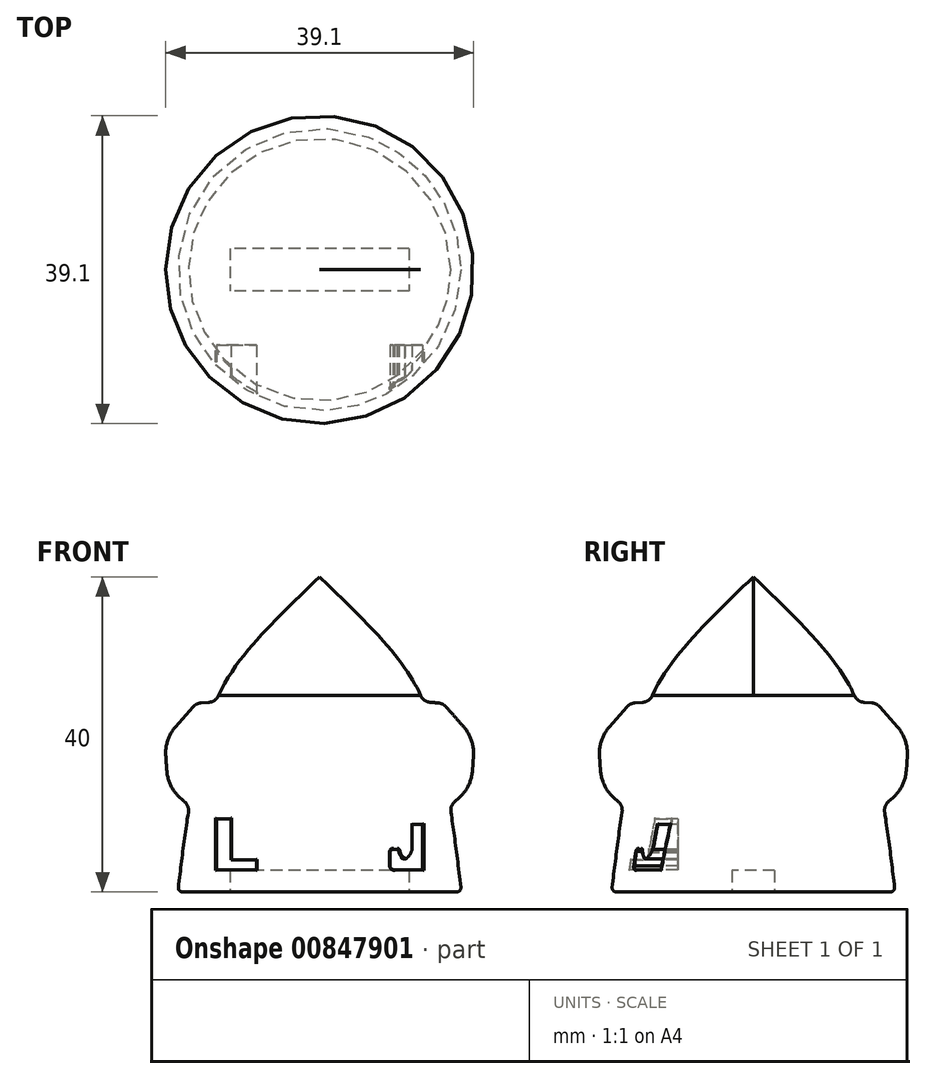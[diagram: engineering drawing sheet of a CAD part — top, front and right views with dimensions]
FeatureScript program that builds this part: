
annotation { "Feature Type Name" : "Feature", "Feature Type Description" : "" }
export const myFeature = defineFeature(function(context is Context, id is Id, definition is map)
    precondition{}
    {
        {
            var Q0;
            Q0=qCreatedBy(makeId("Front.planeOp"),FACE);
            var sketch = newSketch(context, id + "F0", { "sketchPlane" : qUnion([Q0])});
            skLineSegment(sketch, "E0", {"start": v(18, 0) * mm, "end": v(0, 0) * mm});
            skLineSegment(sketch, "E1", {"start": v(0, 40) * mm, "end": v(0, 0) * mm});
            skFitSpline(sketch, "E2", {"points": [v(18, 0) * mm, v(13.4, 23.62) * mm, v(0, 40) * mm], "startDerivative": vector(-8.21, 72.25) * mm, "endDerivative": vector(-57.18, 54.27) * mm});
            skPoint(sketch, "E3.center.orphan", {"position": v(0, 43.03) * mm});
            skFitSpline(sketch, "E4.trimOffspring", {"points": [v(18, 0) * mm, v(13.4, 23.62) * mm, v(0, 40) * mm], "startDerivative": vector(-8.21, 72.25) * mm, "endDerivative": vector(-57.18, 54.27) * mm});
            skArc(sketch, "E5.cCircle", {"start": v(16.55, 10.95) * mm, "mid": v(19.26, 18.64) * mm, "end": v(13.2, 24.1) * mm, "construction": true});
            skLineSegment(sketch, "E5.0", {"start": v(15.66, 23.96) * mm, "end": v(19.67, 19.38) * mm});
            skLineSegment(sketch, "E5.1", {"start": v(19.67, 19.38) * mm, "end": v(19.27, 13.3) * mm});
            skLineSegment(sketch, "E5.2", {"start": v(19.27, 13.3) * mm, "end": v(16.55, 10.93) * mm});
            skLineSegment(sketch, "E5.7", {"start": v(13.2, 24.13) * mm, "end": v(15.66, 23.96) * mm});
            skPoint(sketch, "E5.0.midPoint", {"position": v(17.67, 21.67) * mm});
            skPoint(sketch, "E6.orphan", {"position": v(9.6, 24.36) * mm});
            skSolve(sketch);
        }
        {
            var Q0;
            Q0 = qSketchRegion(id + "F0", true);
            var Q1;
            Q1=sQuery(id+"F0.wireOp",EDGE,"E1");
            revolve(context, id + "F1", {"surfaceOperationType" : NewSurfaceOperationType.NEW, "entities" : qUnion([Q0]), "axis" : qUnion([Q1]), "revolveType" : RevolveType.FULL});
        }
        {
            var Q0;
            Q0=qCreatedBy(makeId("Front.planeOp"),FACE);
            cPlane(context, id + "F2", {"entities" : qUnion([Q0]), "cplaneType" : CPlaneType.OFFSET, "offset" : 25 * mm, "width" : 150 * mm, "height" : 150 * mm});
        }
        {
            var Q0;
            Q0=makeQuery(id+"F1.opRevolve","SWEPT_EDGE",EDGE,{"disambiguationData":[OSD([sQuery(id+"F0.wireOp",EDGE,"E4.trimOffspring"),sQuery(id+"F0.wireOp",EDGE,"E5.7")])]});
            var Q1;
            Q1=makeQuery(id+"F1.opRevolve","SWEPT_EDGE",EDGE,{"disambiguationData":[OSD([sQuery(id+"F0.wireOp",EDGE,"E5.0"),sQuery(id+"F0.wireOp",EDGE,"E5.7")])]});
            var Q2;
            Q2=makeQuery(id+"F1.opRevolve","SWEPT_EDGE",EDGE,{"disambiguationData":[OSD([sQuery(id+"F0.wireOp",EDGE,"E2"),sQuery(id+"F0.wireOp",EDGE,"E5.2")])]});
            fillet(context, id + "F3", {"entities" : qUnion([Q0, Q1, Q2]), "radius" : 1.5 * mm, "tangentPropagation" : true, "allowEdgeOverflow" : false});
        }
        {
            var Q0;
            Q0=makeQuery(id+"F1.opRevolve","SWEPT_EDGE",EDGE,{"disambiguationData":[OSD([sQuery(id+"F0.wireOp",EDGE,"E5.0"),sQuery(id+"F0.wireOp",EDGE,"E5.1")])]});
            var Q1;
            Q1=makeQuery(id+"F1.opRevolve","SWEPT_EDGE",EDGE,{"disambiguationData":[OSD([sQuery(id+"F0.wireOp",EDGE,"E5.1"),sQuery(id+"F0.wireOp",EDGE,"E5.2")])]});
            fillet(context, id + "F4", {"entities" : qUnion([Q0, Q1]), "radius" : 5 * mm, "tangentPropagation" : true, "allowEdgeOverflow" : false});
        }
        {
            var Q0;
            Q0=qCreatedBy(makeId("Top.planeOp"),FACE);
            var sketch = newSketch(context, id + "F5", { "sketchPlane" : qUnion([Q0])});
            skLineSegment(sketch, "E7.bottom", {"start": v(11.37, 2.7) * mm, "end": v(-11.37, 2.7) * mm});
            skLineSegment(sketch, "E7.top", {"start": v(11.37, -2.7) * mm, "end": v(-11.37, -2.7) * mm});
            skLineSegment(sketch, "E7.left", {"start": v(11.37, 2.7) * mm, "end": v(11.37, -2.7) * mm});
            skLineSegment(sketch, "E7.right", {"start": v(-11.37, 2.7) * mm, "end": v(-11.37, -2.7) * mm});
            skPoint(sketch, "E7.middle", {"position": v(0, 0) * mm});
            skSolve(sketch);
        }
        {
            var Q0;
            Q0 = qSketchRegion(id + "F5", true);
            extrude(context, id + "F6", {"entities" : qUnion([Q0]), "operationType" : NewBodyOperationType.REMOVE, "depth" : 2.7 * mm, "offsetDistance" : 25 * mm});
        }
        {
            var Q0;
            Q0=makeQuery(id+"F1.opRevolve","SWEPT_EDGE",EDGE,{"disambiguationData":[OSD([sQuery(id+"F0.wireOp",EDGE,"E0"),sQuery(id+"F0.wireOp",EDGE,"E2")])]});
            fillet(context, id + "F7", {"entities" : qUnion([Q0]), "radius" : .5 * mm, "tangentPropagation" : true, "allowEdgeOverflow" : false});
        }
        {
            var Q0;
            Q0=qCreatedBy(id+"F2.planeOp",FACE);
            var sketch = newSketch(context, id + "F8", { "sketchPlane" : qUnion([Q0])});
            skLineSegment(sketch, "E8", {"start": v(-13.06, 9.29) * mm, "end": v(-11.24, 9.29) * mm});
            skLineSegment(sketch, "E9", {"start": v(-11.24, 9.29) * mm, "end": v(-11.24, 4.03) * mm});
            skLineSegment(sketch, "E10", {"start": v(-11.24, 4.03) * mm, "end": v(-8.02, 4.03) * mm});
            skLineSegment(sketch, "E11", {"start": v(-8.02, 4.03) * mm, "end": v(-8.02, 2.79) * mm});
            skLineSegment(sketch, "E12", {"start": v(-8.02, 2.79) * mm, "end": v(-13.06, 2.79) * mm});
            skLineSegment(sketch, "E13", {"start": v(-13.06, 2.79) * mm, "end": v(-13.06, 9.29) * mm});
            skLineSegment(sketch, "E14", {"start": v(11.74, 8.58) * mm, "end": v(13.08, 8.58) * mm});
            skLineSegment(sketch, "E15", {"start": v(13.08, 8.58) * mm, "end": v(13.08, 2.79) * mm});
            skLineSegment(sketch, "E16", {"start": v(13.08, 2.79) * mm, "end": v(9.48, 2.79) * mm});
            skLineSegment(sketch, "E17", {"start": v(8.94, 3.27) * mm, "end": v(8.94, 5.13) * mm});
            skLineSegment(sketch, "E18", {"start": v(9.35, 5.41) * mm, "end": v(9.84, 5.41) * mm});
            skLineSegment(sketch, "E19", {"start": v(10.86, 4.16) * mm, "end": v(10.86, 4.16) * mm});
            skLineSegment(sketch, "E20", {"start": v(11.74, 8.58) * mm, "end": v(11.74, 5.41) * mm});
            skFitSpline(sketch, "E21", {"points": [v(10, 5.41) * mm, v(10.63, 4.42) * mm, v(10.86, 4.16) * mm, v(11.43, 4.67) * mm, v(11.74, 5.41) * mm], "startDerivative": vector(0.96, -4.15) * mm, "endDerivative": vector(0.74, 3.14) * mm});
            skPoint(sketch, "E22.orphan", {"position": v(11.74, 4.16) * mm});
            skFitSpline(sketch, "E23", {"points": [v(10.1, 4.97) * mm, v(10, 5.31) * mm, v(9.84, 5.41) * mm], "startDerivative": vector(-0.28, 1.01) * mm, "endDerivative": vector(-0.86, 0.1) * mm});
            skFitSpline(sketch, "E24", {"points": [v(9.35, 5.41) * mm, v(9.06, 5.37) * mm, v(8.94, 5.13) * mm], "startDerivative": vector(-0.64, 0.02) * mm, "endDerivative": vector(-0.19, -0.52) * mm});
            skFitSpline(sketch, "E25", {"points": [v(10.1, 4.97) * mm, v(10.39, 4.43) * mm, v(10.52, 4.24) * mm, v(10.66, 4.2) * mm, v(10.86, 4.16) * mm], "startDerivative": vector(0.34, -1.84) * mm, "endDerivative": vector(0.93, -0.07) * mm});
            skFitSpline(sketch, "E26", {"points": [v(8.94, 3.27) * mm, v(9.07, 2.96) * mm, v(9.48, 2.79) * mm, v(9.52, 2.79) * mm], "startDerivative": vector(0.11, -0.84) * mm, "endDerivative": vector(0.21, 0.04) * mm});
            skPoint(sketch, "E27.orphan", {"position": v(-15.44, 9.29) * mm});
            skSolve(sketch);
        }
        {
            var Q0;
            Q0 = qSketchRegion(id + "F8", true);
            extrude(context, id + "F9", {"entities" : qUnion([Q0]), "operationType" : NewBodyOperationType.REMOVE, "oppositeDirection" : true, "depth" : 15.4 * mm, "offsetDistance" : 25 * mm});
        }
        {
            var Q0;
            Q0=makeQuery(id+"F9.boolean.opBoolean","INTERSECT",EDGE,{"derivedFrom":[makeQuery(id+"F1.opRevolve","SWEPT_FACE",FACE,{"disambiguationData":[OSD([sQuery(id+"F0.wireOp",EDGE,"E2")])]}),makeQuery(id+"F9.opExtrude","SWEPT_FACE",FACE,{"disambiguationData":[OSD([sQuery(id+"F8.wireOp",EDGE,"E9")])]})]});
            var Q1;
            Q1=makeQuery(id+"F9.boolean.opBoolean","INTERSECT",EDGE,{"derivedFrom":[makeQuery(id+"F1.opRevolve","SWEPT_FACE",FACE,{"disambiguationData":[OSD([sQuery(id+"F0.wireOp",EDGE,"E2")])]}),makeQuery(id+"F9.opExtrude","SWEPT_FACE",FACE,{"disambiguationData":[OSD([sQuery(id+"F8.wireOp",EDGE,"E10")])]})]});
            var Q2;
            Q2=makeQuery(id+"F9.boolean.opBoolean","INTERSECT",EDGE,{"derivedFrom":[makeQuery(id+"F1.opRevolve","SWEPT_FACE",FACE,{"disambiguationData":[OSD([sQuery(id+"F0.wireOp",EDGE,"E2")])]}),makeQuery(id+"F9.opExtrude","SWEPT_FACE",FACE,{"disambiguationData":[OSD([sQuery(id+"F8.wireOp",EDGE,"E11")])]})]});
            var Q3;
            Q3=makeQuery(id+"F9.boolean.opBoolean","INTERSECT",EDGE,{"derivedFrom":[makeQuery(id+"F1.opRevolve","SWEPT_FACE",FACE,{"disambiguationData":[OSD([sQuery(id+"F0.wireOp",EDGE,"E2")])]}),makeQuery(id+"F9.opExtrude","SWEPT_FACE",FACE,{"disambiguationData":[OSD([sQuery(id+"F8.wireOp",EDGE,"E12")])]})]});
            var Q4;
            Q4=makeQuery(id+"F9.boolean.opBoolean","INTERSECT",EDGE,{"derivedFrom":[makeQuery(id+"F1.opRevolve","SWEPT_FACE",FACE,{"disambiguationData":[OSD([sQuery(id+"F0.wireOp",EDGE,"E2")])]}),makeQuery(id+"F9.opExtrude","SWEPT_FACE",FACE,{"disambiguationData":[OSD([sQuery(id+"F8.wireOp",EDGE,"E13")])]})]});
            var Q5;
            Q5=makeQuery(id+"F9.boolean.opBoolean","INTERSECT",EDGE,{"derivedFrom":[makeQuery(id+"F1.opRevolve","SWEPT_FACE",FACE,{"disambiguationData":[OSD([sQuery(id+"F0.wireOp",EDGE,"E2")])]}),makeQuery(id+"F9.opExtrude","SWEPT_FACE",FACE,{"disambiguationData":[OSD([sQuery(id+"F8.wireOp",EDGE,"E8")])]})]});
            var Q6;
            Q6=makeQuery(id+"F9.boolean.opBoolean","INTERSECT",EDGE,{"derivedFrom":[makeQuery(id+"F1.opRevolve","SWEPT_FACE",FACE,{"disambiguationData":[OSD([sQuery(id+"F0.wireOp",EDGE,"E2")])]}),makeQuery(id+"F9.opExtrude","SWEPT_FACE",FACE,{"disambiguationData":[OSD([sQuery(id+"F8.wireOp",EDGE,"E20")])]})]});
            var Q7;
            Q7=makeQuery(id+"F9.boolean.opBoolean","INTERSECT",EDGE,{"derivedFrom":[makeQuery(id+"F1.opRevolve","SWEPT_FACE",FACE,{"disambiguationData":[OSD([sQuery(id+"F0.wireOp",EDGE,"E2")])]}),makeQuery(id+"F9.opExtrude","SWEPT_FACE",FACE,{"disambiguationData":[OSD([sQuery(id+"F8.wireOp",EDGE,"E25")])]})]});
            var Q8;
            Q8=makeQuery(id+"F9.boolean.opBoolean","INTERSECT",EDGE,{"derivedFrom":[makeQuery(id+"F1.opRevolve","SWEPT_FACE",FACE,{"disambiguationData":[OSD([sQuery(id+"F0.wireOp",EDGE,"E2")])]}),makeQuery(id+"F9.opExtrude","SWEPT_FACE",FACE,{"disambiguationData":[OSD([sQuery(id+"F8.wireOp",EDGE,"E23")])]})]});
            var Q9;
            Q9=makeQuery(id+"F9.boolean.opBoolean","INTERSECT",EDGE,{"derivedFrom":[makeQuery(id+"F1.opRevolve","SWEPT_FACE",FACE,{"disambiguationData":[OSD([sQuery(id+"F0.wireOp",EDGE,"E2")])]}),makeQuery(id+"F9.opExtrude","SWEPT_FACE",FACE,{"disambiguationData":[OSD([sQuery(id+"F8.wireOp",EDGE,"E18")])]})]});
            var Q10;
            Q10=makeQuery(id+"F9.boolean.opBoolean","INTERSECT",EDGE,{"derivedFrom":[makeQuery(id+"F1.opRevolve","SWEPT_FACE",FACE,{"disambiguationData":[OSD([sQuery(id+"F0.wireOp",EDGE,"E2")])]}),makeQuery(id+"F9.opExtrude","SWEPT_FACE",FACE,{"disambiguationData":[OSD([sQuery(id+"F8.wireOp",EDGE,"E24")])]})]});
            var Q11;
            Q11=makeQuery(id+"F9.boolean.opBoolean","INTERSECT",EDGE,{"derivedFrom":[makeQuery(id+"F1.opRevolve","SWEPT_FACE",FACE,{"disambiguationData":[OSD([sQuery(id+"F0.wireOp",EDGE,"E2")])]}),makeQuery(id+"F9.opExtrude","SWEPT_FACE",FACE,{"disambiguationData":[OSD([sQuery(id+"F8.wireOp",EDGE,"E17")])]})]});
            var Q12;
            Q12=makeQuery(id+"F9.boolean.opBoolean","INTERSECT",EDGE,{"derivedFrom":[makeQuery(id+"F1.opRevolve","SWEPT_FACE",FACE,{"disambiguationData":[OSD([sQuery(id+"F0.wireOp",EDGE,"E2")])]}),makeQuery(id+"F9.opExtrude","SWEPT_FACE",FACE,{"disambiguationData":[OSD([sQuery(id+"F8.wireOp",EDGE,"E16")])]})]});
            var Q13;
            Q13=makeQuery(id+"F9.boolean.opBoolean","INTERSECT",EDGE,{"derivedFrom":[makeQuery(id+"F1.opRevolve","SWEPT_FACE",FACE,{"disambiguationData":[OSD([sQuery(id+"F0.wireOp",EDGE,"E2")])]}),makeQuery(id+"F9.opExtrude","SWEPT_FACE",FACE,{"disambiguationData":[OSD([sQuery(id+"F8.wireOp",EDGE,"E26")])]})]});
            var Q14;
            Q14=makeQuery(id+"F9.boolean.opBoolean","INTERSECT",EDGE,{"derivedFrom":[makeQuery(id+"F1.opRevolve","SWEPT_FACE",FACE,{"disambiguationData":[OSD([sQuery(id+"F0.wireOp",EDGE,"E2")])]}),makeQuery(id+"F9.opExtrude","SWEPT_FACE",FACE,{"disambiguationData":[OSD([sQuery(id+"F8.wireOp",EDGE,"E15")])]})]});
            var Q15;
            Q15=makeQuery(id+"F9.boolean.opBoolean","INTERSECT",EDGE,{"derivedFrom":[makeQuery(id+"F1.opRevolve","SWEPT_FACE",FACE,{"disambiguationData":[OSD([sQuery(id+"F0.wireOp",EDGE,"E2")])]}),makeQuery(id+"F9.opExtrude","SWEPT_FACE",FACE,{"disambiguationData":[OSD([sQuery(id+"F8.wireOp",EDGE,"E14")])]})]});
            fillet(context, id + "F10", {"entities" : qUnion([Q0, Q1, Q2, Q3, Q4, Q5, Q6, Q7, Q8, Q9, Q10, Q11, Q12, Q13, Q14, Q15]), "radius" : .1 * mm, "tangentPropagation" : true, "allowEdgeOverflow" : false});
        }
    });
